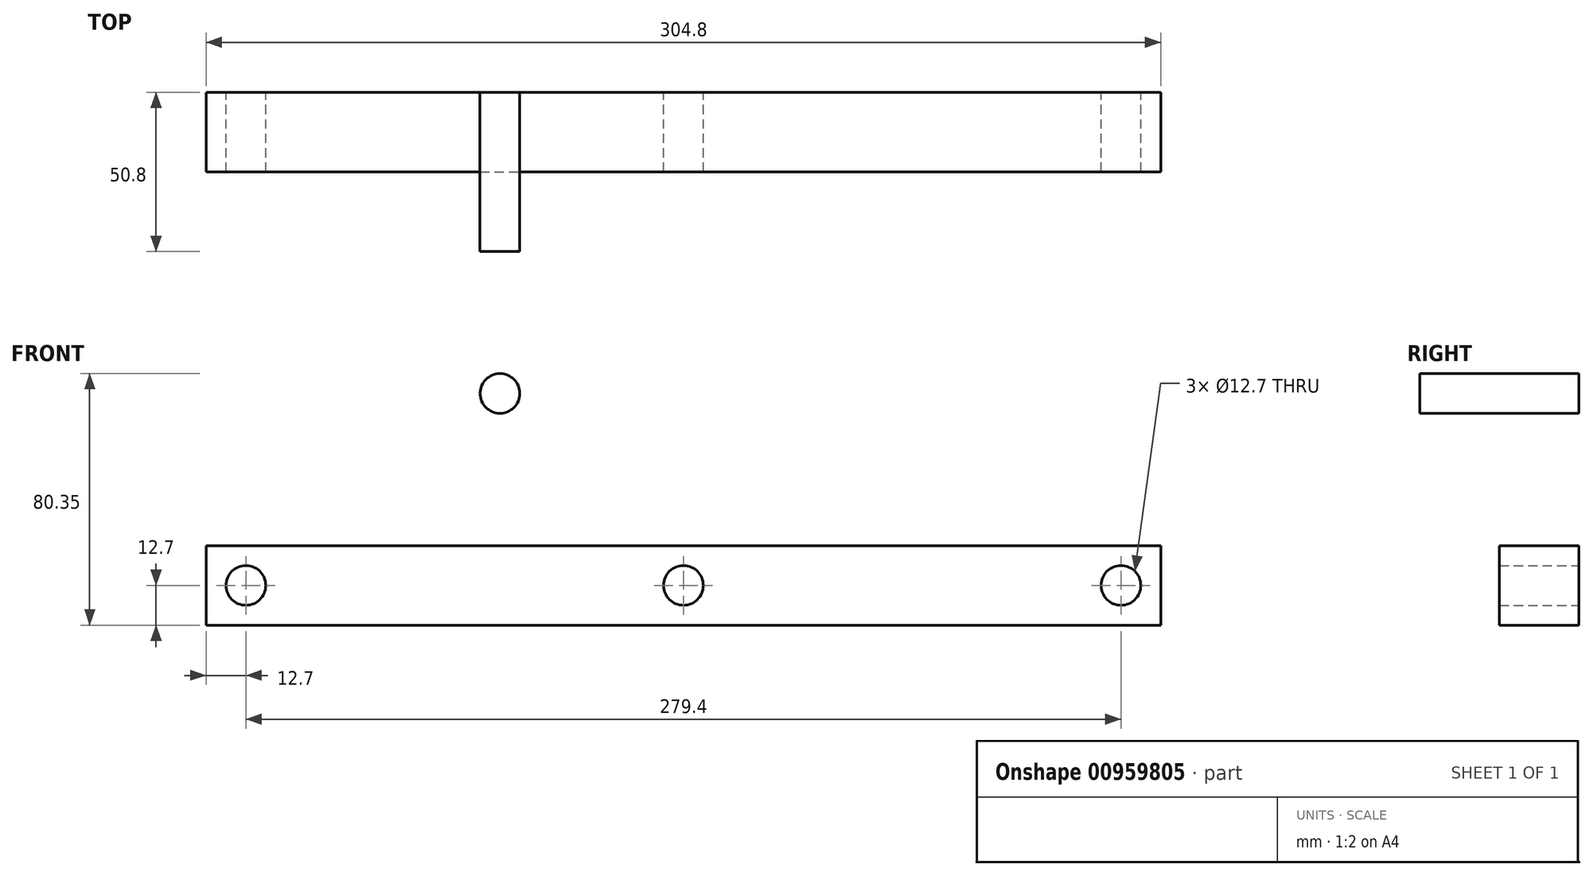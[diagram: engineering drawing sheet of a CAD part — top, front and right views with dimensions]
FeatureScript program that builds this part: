
annotation { "Feature Type Name" : "Feature", "Feature Type Description" : "" }
export const myFeature = defineFeature(function(context is Context, id is Id, definition is map)
    precondition{}
    {
        {
            var Q0;
            Q0=qCreatedBy(makeId("Front.planeOp"),FACE);
            var sketch = newSketch(context, id + "F0", { "sketchPlane" : qUnion([Q0])});
            skLineSegment(sketch, "E0.bottom", {"start": v(-152.4, 12.7) * mm, "end": v(152.4, 12.7) * mm});
            skLineSegment(sketch, "E0.top", {"start": v(-152.4, -12.7) * mm, "end": v(152.4, -12.7) * mm});
            skLineSegment(sketch, "E0.left", {"start": v(-152.4, 12.7) * mm, "end": v(-152.4, -12.7) * mm});
            skLineSegment(sketch, "E0.right", {"start": v(152.4, 12.7) * mm, "end": v(152.4, -12.7) * mm});
            skPoint(sketch, "E0.middle", {"position": v(0, 0) * mm});
            skCircle(sketch, "E1", {"center": v(-139.7, 0) * mm, "radius": 6.35 * mm});
            skLineSegment(sketch, "E2", {"start": v(0, 12.7) * mm, "end": v(0, 62.85) * mm});
            skLineSegment(sketch, "E3.MirrorCS", {"start": v(152.4, 12.7) * mm, "end": v(-152.4, 12.7) * mm});
            skCircle(sketch, "E4.MirrorC", {"center": v(139.7, 0) * mm, "radius": 6.35 * mm});
            skLineSegment(sketch, "E5.MirrorCS", {"start": v(152.4, -12.7) * mm, "end": v(-152.4, -12.7) * mm});
            skCircle(sketch, "E6", {"center": v(0, 0) * mm, "radius": 6.35 * mm});
            skSolve(sketch);
        }
        {
            var Q0;
            Q0 = qSketchRegion(id + "F0", true);
            extrude(context, id + "F1", {"entities" : qUnion([Q0]), "depth" : 25.4 * mm, "offsetDistance" : 25.4 * mm});
        }
        {
            var Q0;
            Q0=qCreatedBy(makeId("Front.planeOp"),FACE);
            var sketch = newSketch(context, id + "F2", { "sketchPlane" : qUnion([Q0])});
            skCircle(sketch, "E7", {"center": v(-58.57, 61.3) * mm, "radius": 6.35 * mm});
            skSolve(sketch);
        }
        {
            var Q0;
            Q0=makeQuery(id+"F2.imprint","IMPRINT",FACE,{"disambiguationData":[TD([[makeQuery(id+"F2.imprint","IMPRINT",EDGE,{"derivedFrom":sQuery(id+"F2.wireOp",EDGE,"E7")}),1.0]])]});
            extrude(context, id + "F3", {"entities" : qUnion([Q0]), "depth" : 50.8 * mm, "offsetDistance" : 25.4 * mm});
        }
    });
